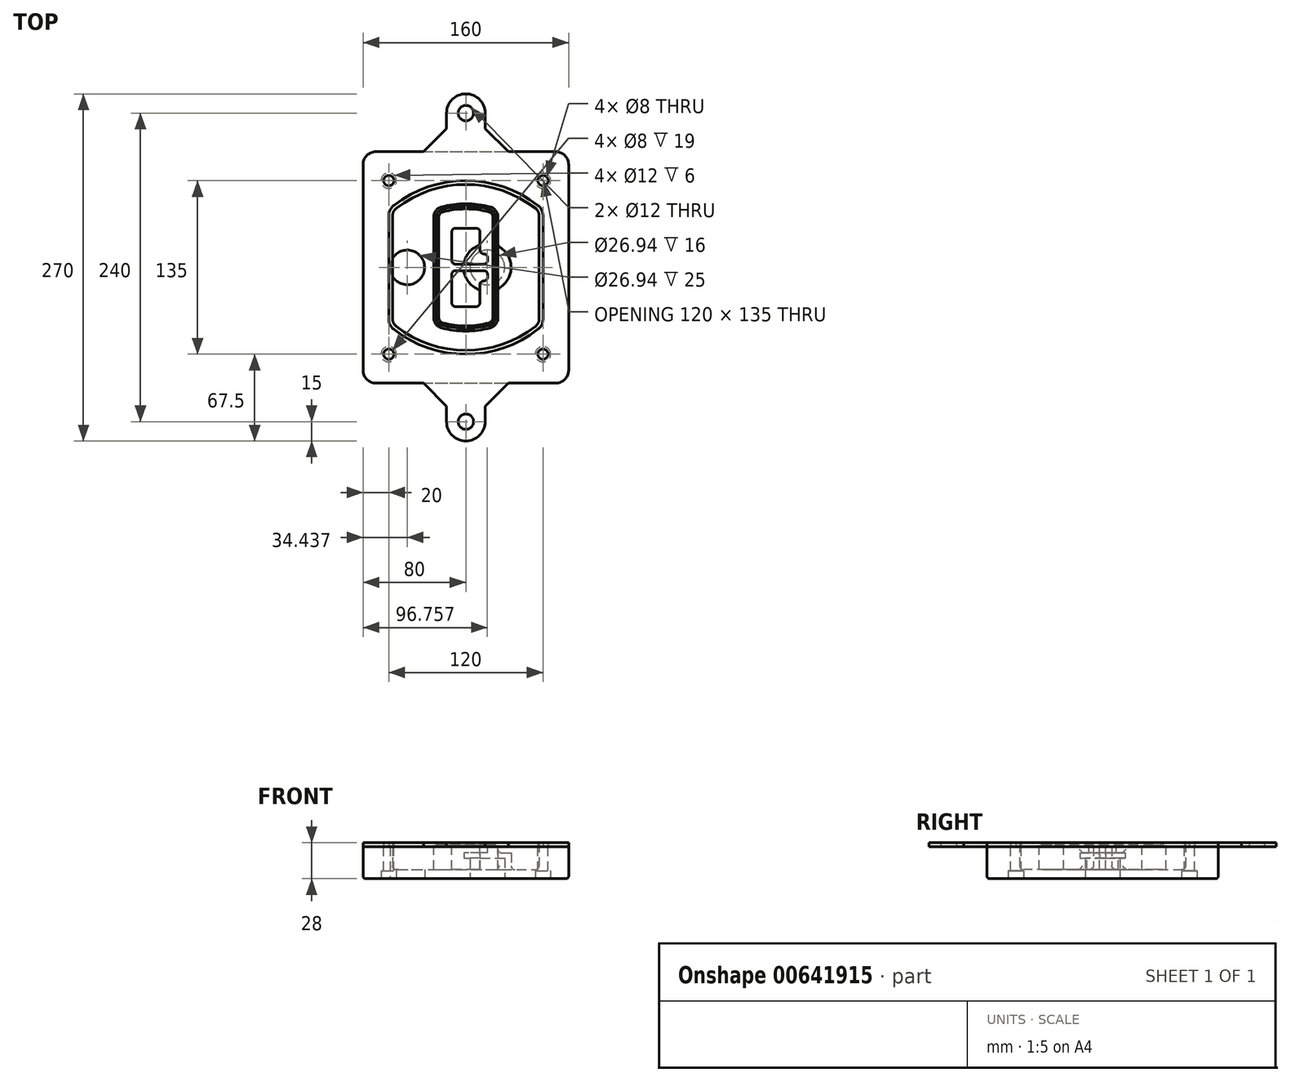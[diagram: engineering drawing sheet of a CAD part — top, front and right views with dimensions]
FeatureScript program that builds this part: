
annotation { "Feature Type Name" : "Feature", "Feature Type Description" : "" }
export const myFeature = defineFeature(function(context is Context, id is Id, definition is map)
    precondition{}
    {
        {
            var Q0;
            Q0=qCreatedBy(makeId("Top.planeOp"),FACE);
            var sketch = newSketch(context, id + "F0", { "sketchPlane" : qUnion([Q0])});
            skPoint(sketch, "E0.rect.middle", {"position": v(0, 0) * mm});
            skLineSegment(sketch, "E1.bottom", {"start": v(-70, -90) * mm, "end": v(70, -90) * mm});
            skLineSegment(sketch, "E1.top", {"start": v(-70, 90) * mm, "end": v(70, 90) * mm});
            skLineSegment(sketch, "E1.left", {"start": v(-80, -80) * mm, "end": v(-80, 80) * mm});
            skLineSegment(sketch, "E1.right", {"start": v(80, -80) * mm, "end": v(80, 80) * mm});
            skLineSegment(sketch, "E2", {"start": v(-80, 90) * mm, "end": v(80, -90) * mm, "construction": true});
            skLineSegment(sketch, "E3", {"start": v(80, 90) * mm, "end": v(-80, -90) * mm, "construction": true});
            skCircle(sketch, "E4", {"center": v(-60, 67.5) * mm, "radius": 4 * mm});
            skCircle(sketch, "E5", {"center": v(60, 67.5) * mm, "radius": 4 * mm});
            skCircle(sketch, "E6", {"center": v(60, -67.5) * mm, "radius": 4 * mm});
            skCircle(sketch, "E7", {"center": v(-60, -67.5) * mm, "radius": 4 * mm});
            skLineSegment(sketch, "E8", {"start": v(-60, 67.5) * mm, "end": v(60, 67.5) * mm, "construction": true});
            skLineSegment(sketch, "E9", {"start": v(60, 67.5) * mm, "end": v(60, -67.5) * mm, "construction": true});
            skLineSegment(sketch, "E10", {"start": v(60, -67.5) * mm, "end": v(-60, -67.5) * mm, "construction": true});
            skLineSegment(sketch, "E11", {"start": v(-60, -67.5) * mm, "end": v(-60, 67.5) * mm, "construction": true});
            skLineSegment(sketch, "E12", {"start": v(-60, 40.3) * mm, "end": v(-60, -40.3) * mm});
            skLineSegment(sketch, "E13", {"start": v(60, 40.3) * mm, "end": v(60, -40.3) * mm});
            skArc(sketch, "E14", {"start": v(56.15, 48.18) * mm, "mid": v(0, 67.5) * mm, "end": v(-56.15, 48.18) * mm});
            skArc(sketch, "E15", {"start": v(-56.15, -48.18) * mm, "mid": v(0, -67.5) * mm, "end": v(56.15, -48.18) * mm});
            skLineSegment(sketch, "E16", {"start": v(-60, 0) * mm, "end": v(60, 0) * mm, "construction": true});
            skPoint(sketch, "E17.visualSharp", {"position": v(-60, -45) * mm});
            skArc(sketch, "E17.filletArc", {"start": v(-60, -40.3) * mm, "mid": v(-58.99, -44.68) * mm, "end": v(-56.15, -48.18) * mm});
            skPoint(sketch, "E18.visualSharp", {"position": v(-60, 45) * mm});
            skArc(sketch, "E18.filletArc", {"start": v(-56.15, 48.18) * mm, "mid": v(-58.99, 44.68) * mm, "end": v(-60, 40.3) * mm});
            skPoint(sketch, "E19.visualSharp", {"position": v(60, 45) * mm});
            skArc(sketch, "E19.filletArc", {"start": v(60, 40.3) * mm, "mid": v(58.99, 44.68) * mm, "end": v(56.15, 48.18) * mm});
            skPoint(sketch, "E20.visualSharp", {"position": v(60, -45) * mm});
            skArc(sketch, "E20.filletArc", {"start": v(56.15, -48.18) * mm, "mid": v(58.99, -44.68) * mm, "end": v(60, -40.3) * mm});
            skPoint(sketch, "E21.visualSharp", {"position": v(-80, 90) * mm});
            skArc(sketch, "E21.filletArc", {"start": v(-70, 90) * mm, "mid": v(-77.07, 87.07) * mm, "end": v(-80, 80) * mm});
            skPoint(sketch, "E22.visualSharp", {"position": v(80, 90) * mm});
            skArc(sketch, "E22.filletArc", {"start": v(80, 80) * mm, "mid": v(77.07, 87.07) * mm, "end": v(70, 90) * mm});
            skPoint(sketch, "E23.visualSharp", {"position": v(80, -90) * mm});
            skArc(sketch, "E23.filletArc", {"start": v(70, -90) * mm, "mid": v(77.07, -87.07) * mm, "end": v(80, -80) * mm});
            skPoint(sketch, "E24.visualSharp", {"position": v(-80, -90) * mm});
            skArc(sketch, "E24.filletArc", {"start": v(-80, -80) * mm, "mid": v(-77.07, -87.07) * mm, "end": v(-70, -90) * mm});
            skArc(sketch, "E25.0", {"start": v(57, 40.3) * mm, "mid": v(56.3, 43.36) * mm, "end": v(54.3, 45.81) * mm});
            skLineSegment(sketch, "E25.1", {"start": v(57, 40.3) * mm, "end": v(57, -40.3) * mm});
            skArc(sketch, "E25.2", {"start": v(54.3, -45.81) * mm, "mid": v(56.3, -43.36) * mm, "end": v(57, -40.3) * mm});
            skArc(sketch, "E25.3", {"start": v(-54.3, -45.81) * mm, "mid": v(0, -64.5) * mm, "end": v(54.3, -45.81) * mm});
            skArc(sketch, "E25.4", {"start": v(-57, -40.3) * mm, "mid": v(-56.3, -43.36) * mm, "end": v(-54.3, -45.81) * mm});
            skArc(sketch, "E25.5", {"start": v(54.3, 45.81) * mm, "mid": v(0, 64.5) * mm, "end": v(-54.3, 45.81) * mm});
            skLineSegment(sketch, "E25.6", {"start": v(-57, 40.3) * mm, "end": v(-57, -40.3) * mm});
            skArc(sketch, "E25.7", {"start": v(-54.3, 45.81) * mm, "mid": v(-56.3, 43.36) * mm, "end": v(-57, 40.3) * mm});
            skArc(sketch, "E26.0", {"start": v(-58.62, 51.33) * mm, "mid": v(-62.58, 46.43) * mm, "end": v(-64, 40.3) * mm});
            skArc(sketch, "E26.1", {"start": v(58.62, 51.33) * mm, "mid": v(0, 71.5) * mm, "end": v(-58.62, 51.33) * mm});
            skArc(sketch, "E26.2", {"start": v(64, 40.3) * mm, "mid": v(62.58, 46.43) * mm, "end": v(58.62, 51.33) * mm});
            skLineSegment(sketch, "E26.3", {"start": v(64, 40.3) * mm, "end": v(64, -40.3) * mm});
            skArc(sketch, "E26.4", {"start": v(58.62, -51.33) * mm, "mid": v(62.58, -46.43) * mm, "end": v(64, -40.3) * mm});
            skLineSegment(sketch, "E26.5", {"start": v(-64, 40.3) * mm, "end": v(-64, -40.3) * mm});
            skArc(sketch, "E26.6", {"start": v(-58.62, -51.33) * mm, "mid": v(0, -71.5) * mm, "end": v(58.62, -51.33) * mm});
            skArc(sketch, "E26.7", {"start": v(-64, -40.3) * mm, "mid": v(-62.58, -46.43) * mm, "end": v(-58.62, -51.33) * mm});
            skSolve(sketch);
        }
        {
            var Q0;
            Q0=makeQuery(id+"F0.imprint","IMPRINT",FACE,{"disambiguationData":[TD([[makeQuery(id+"F0.imprint","IMPRINT",EDGE,{"derivedFrom":sQuery(id+"F0.wireOp",EDGE,"E1.bottom")}),1.0]])]});
            var Q1;
            Q1=makeQuery(id+"F0.imprint","IMPRINT",FACE,{"disambiguationData":[TD([[makeQuery(id+"F0.imprint","IMPRINT",EDGE,{"derivedFrom":sQuery(id+"F0.wireOp",EDGE,"E12")}),1.0]])]});
            var Q2;
            Q2=makeQuery(id+"F0.imprint","IMPRINT",FACE,{"disambiguationData":[TD([[makeQuery(id+"F0.imprint","IMPRINT",EDGE,{"derivedFrom":sQuery(id+"F0.wireOp",EDGE,"E25.0")}),1.0]])]});
            var Q3;
            Q3=makeQuery(id+"F0.imprint","IMPRINT",FACE,{"disambiguationData":[TD([[makeQuery(id+"F0.imprint","IMPRINT",EDGE,{"derivedFrom":sQuery(id+"F0.wireOp",EDGE,"E12")}),-1.0]])]});
            extrude(context, id + "F1", {"entities" : qUnion([Q0, Q1, Q2, Q3]), "oppositeDirection" : true, "depth" : 25 * mm});
        }
        {
            var Q0;
            Q0=makeQuery(id+"F0.imprint","IMPRINT",FACE,{"disambiguationData":[TD([[makeQuery(id+"F0.imprint","IMPRINT",EDGE,{"derivedFrom":sQuery(id+"F0.wireOp",EDGE,"E12")}),1.0]])]});
            extrude(context, id + "F2", {"entities" : qUnion([Q0]), "operationType" : NewBodyOperationType.ADD, "depth" : 3 * mm});
        }
        {
            var Q0;
            Q0=makeQuery(id+"F0.imprint","IMPRINT",FACE,{"disambiguationData":[TD([[makeQuery(id+"F0.imprint","IMPRINT",EDGE,{"derivedFrom":sQuery(id+"F0.wireOp",EDGE,"E25.0")}),1.0]])]});
            extrude(context, id + "F3", {"entities" : qUnion([Q0]), "operationType" : NewBodyOperationType.REMOVE, "oppositeDirection" : true, "depth" : 18 * mm});
        }
        {
            var Q0;
            Q0=makeQuery(id+"F2.opExtrude","CAP_FACE",FACE,{"disambiguationData":[OSD([sQuery(id+"F0.wireOp",EDGE,"E12"),sQuery(id+"F0.wireOp",EDGE,"E13"),sQuery(id+"F0.wireOp",EDGE,"E14"),sQuery(id+"F0.wireOp",EDGE,"E15"),sQuery(id+"F0.wireOp",EDGE,"E17.filletArc"),sQuery(id+"F0.wireOp",EDGE,"E18.filletArc"),sQuery(id+"F0.wireOp",EDGE,"E19.filletArc"),sQuery(id+"F0.wireOp",EDGE,"E20.filletArc"),sQuery(id+"F0.wireOp",EDGE,"E25.0"),sQuery(id+"F0.wireOp",EDGE,"E25.1"),sQuery(id+"F0.wireOp",EDGE,"E25.2"),sQuery(id+"F0.wireOp",EDGE,"E25.3"),sQuery(id+"F0.wireOp",EDGE,"E25.4"),sQuery(id+"F0.wireOp",EDGE,"E25.5"),sQuery(id+"F0.wireOp",EDGE,"E25.6"),sQuery(id+"F0.wireOp",EDGE,"E25.7")])],"isStart":false});
            var sketch = newSketch(context, id + "F4", { "sketchPlane" : qUnion([Q0])});
            skArc(sketch, "E27.0", {"start": v(-19.08, -46.97) * mm, "mid": v(0, -49.5) * mm, "end": v(19.08, -46.97) * mm});
            skArc(sketch, "E28.0", {"start": v(19.08, 46.97) * mm, "mid": v(0, 49.5) * mm, "end": v(-19.08, 46.97) * mm});
            skLineSegment(sketch, "E29", {"start": v(-25, 39.25) * mm, "end": v(-25, -39.25) * mm});
            skLineSegment(sketch, "E30", {"start": v(25, 39.25) * mm, "end": v(25, -39.25) * mm});
            skLineSegment(sketch, "E31", {"start": v(-25, 45.1) * mm, "end": v(25, 45.1) * mm, "construction": true});
            skLineSegment(sketch, "E32", {"start": v(-25, -45.1) * mm, "end": v(25, -45.1) * mm, "construction": true});
            skPoint(sketch, "E33.visualSharp", {"position": v(-25, 45.1) * mm});
            skArc(sketch, "E33.filletArc", {"start": v(-19.08, 46.97) * mm, "mid": v(-23.35, 44.11) * mm, "end": v(-25, 39.25) * mm});
            skPoint(sketch, "E34.visualSharp", {"position": v(25, 45.1) * mm});
            skArc(sketch, "E34.filletArc", {"start": v(25, 39.25) * mm, "mid": v(23.35, 44.11) * mm, "end": v(19.08, 46.97) * mm});
            skPoint(sketch, "E35.visualSharp", {"position": v(25, -45.1) * mm});
            skArc(sketch, "E35.filletArc", {"start": v(19.08, -46.97) * mm, "mid": v(23.35, -44.11) * mm, "end": v(25, -39.25) * mm});
            skPoint(sketch, "E36.visualSharp", {"position": v(-25, -45.1) * mm});
            skArc(sketch, "E36.filletArc", {"start": v(-25, -39.25) * mm, "mid": v(-23.35, -44.11) * mm, "end": v(-19.08, -46.97) * mm});
            skArc(sketch, "E37.0", {"start": v(54.3, 45.81) * mm, "mid": v(0, 64.5) * mm, "end": v(-54.3, 45.81) * mm});
            skArc(sketch, "E37.1", {"start": v(-54.3, 45.81) * mm, "mid": v(-56.3, 43.36) * mm, "end": v(-57, 40.3) * mm});
            skLineSegment(sketch, "E37.2", {"start": v(-57, 40.3) * mm, "end": v(-57, -40.3) * mm});
            skArc(sketch, "E37.3", {"start": v(-57, -40.3) * mm, "mid": v(-56.3, -43.36) * mm, "end": v(-54.3, -45.81) * mm});
            skArc(sketch, "E37.4", {"start": v(-54.3, -45.81) * mm, "mid": v(0, -64.5) * mm, "end": v(54.3, -45.81) * mm});
            skArc(sketch, "E37.5", {"start": v(54.3, -45.81) * mm, "mid": v(56.3, -43.36) * mm, "end": v(57, -40.3) * mm});
            skLineSegment(sketch, "E37.6", {"start": v(57, 40.3) * mm, "end": v(57, -40.3) * mm});
            skArc(sketch, "E37.7", {"start": v(57, 40.3) * mm, "mid": v(56.3, 43.36) * mm, "end": v(54.3, 45.81) * mm});
            skLineSegment(sketch, "E38.0", {"start": v(23, 39.25) * mm, "end": v(23, -39.25) * mm});
            skArc(sketch, "E38.1", {"start": v(18.56, -45.04) * mm, "mid": v(21.76, -42.9) * mm, "end": v(23, -39.25) * mm});
            skArc(sketch, "E38.2", {"start": v(-18.56, -45.04) * mm, "mid": v(0, -47.5) * mm, "end": v(18.56, -45.04) * mm});
            skArc(sketch, "E38.3", {"start": v(-23, -39.25) * mm, "mid": v(-21.76, -42.9) * mm, "end": v(-18.56, -45.04) * mm});
            skLineSegment(sketch, "E38.4", {"start": v(-23, 39.25) * mm, "end": v(-23, -39.25) * mm});
            skArc(sketch, "E38.5", {"start": v(23, 39.25) * mm, "mid": v(21.76, 42.9) * mm, "end": v(18.56, 45.04) * mm});
            skArc(sketch, "E38.6", {"start": v(-18.56, 45.04) * mm, "mid": v(-21.76, 42.9) * mm, "end": v(-23, 39.25) * mm});
            skArc(sketch, "E38.7", {"start": v(18.56, 45.04) * mm, "mid": v(0, 47.5) * mm, "end": v(-18.56, 45.04) * mm});
            skArc(sketch, "E39.0", {"start": v(21, 39.25) * mm, "mid": v(20.18, 41.68) * mm, "end": v(18.04, 43.1) * mm});
            skLineSegment(sketch, "E39.1", {"start": v(21, 39.25) * mm, "end": v(21, -39.25) * mm});
            skArc(sketch, "E39.2", {"start": v(18.04, -43.1) * mm, "mid": v(20.18, -41.68) * mm, "end": v(21, -39.25) * mm});
            skArc(sketch, "E39.3", {"start": v(-18.04, -43.1) * mm, "mid": v(0, -45.5) * mm, "end": v(18.04, -43.1) * mm});
            skArc(sketch, "E39.4", {"start": v(-21, -39.25) * mm, "mid": v(-20.18, -41.68) * mm, "end": v(-18.04, -43.1) * mm});
            skArc(sketch, "E39.5", {"start": v(18.04, 43.1) * mm, "mid": v(0, 45.5) * mm, "end": v(-18.04, 43.1) * mm});
            skLineSegment(sketch, "E39.6", {"start": v(-21, 39.25) * mm, "end": v(-21, -39.25) * mm});
            skArc(sketch, "E39.7", {"start": v(-18.04, 43.1) * mm, "mid": v(-20.18, 41.68) * mm, "end": v(-21, 39.25) * mm});
            skLineSegment(sketch, "E40", {"start": v(-25, 0) * mm, "end": v(25, 0) * mm, "construction": true});
            skLineSegment(sketch, "E41", {"start": v(-11, 5.5) * mm, "end": v(-11, 27.5) * mm});
            skLineSegment(sketch, "E42", {"start": v(-8, 30.5) * mm, "end": v(8, 30.5) * mm});
            skLineSegment(sketch, "E43", {"start": v(11, 27.5) * mm, "end": v(11, 13.5) * mm});
            skLineSegment(sketch, "E44", {"start": v(14, 10.5) * mm, "end": v(14, 10.5) * mm});
            skLineSegment(sketch, "E45", {"start": v(17, 7.5) * mm, "end": v(17, 5.5) * mm});
            skLineSegment(sketch, "E46", {"start": v(14, 2.5) * mm, "end": v(-8, 2.5) * mm});
            skPoint(sketch, "E47.visualSharp", {"position": v(-11, 30.5) * mm});
            skArc(sketch, "E47.filletArc", {"start": v(-8, 30.5) * mm, "mid": v(-10.12, 29.62) * mm, "end": v(-11, 27.5) * mm});
            skPoint(sketch, "E48.visualSharp", {"position": v(11, 30.5) * mm});
            skArc(sketch, "E48.filletArc", {"start": v(11, 27.5) * mm, "mid": v(10.12, 29.62) * mm, "end": v(8, 30.5) * mm});
            skPoint(sketch, "E49.visualSharp", {"position": v(11, 10.5) * mm});
            skArc(sketch, "E49.filletArc", {"start": v(11, 13.5) * mm, "mid": v(11.88, 11.38) * mm, "end": v(14, 10.5) * mm});
            skPoint(sketch, "E50.visualSharp", {"position": v(17, 10.5) * mm});
            skArc(sketch, "E50.filletArc", {"start": v(17, 7.5) * mm, "mid": v(16.12, 9.62) * mm, "end": v(14, 10.5) * mm});
            skPoint(sketch, "E51.visualSharp", {"position": v(17, 2.5) * mm});
            skArc(sketch, "E51.filletArc", {"start": v(14, 2.5) * mm, "mid": v(16.12, 3.38) * mm, "end": v(17, 5.5) * mm});
            skPoint(sketch, "E52.visualSharp", {"position": v(-11, 2.5) * mm});
            skArc(sketch, "E52.filletArc", {"start": v(-11, 5.5) * mm, "mid": v(-10.12, 3.38) * mm, "end": v(-8, 2.5) * mm});
            skLineSegment(sketch, "E53.0.MirrorCS", {"start": v(14, -2.5) * mm, "end": v(-8, -2.5) * mm});
            skArc(sketch, "E54.0.MirrorCS", {"start": v(-11, -5.5) * mm, "mid": v(-10.12, -3.38) * mm, "end": v(-8, -2.5) * mm});
            skLineSegment(sketch, "E55.0.MirrorCS", {"start": v(-11, -5.5) * mm, "end": v(-11, -27.5) * mm});
            skArc(sketch, "E56.0.MirrorCS", {"start": v(-8, -30.5) * mm, "mid": v(-10.12, -29.62) * mm, "end": v(-11, -27.5) * mm});
            skLineSegment(sketch, "E57.0.MirrorCS", {"start": v(-8, -30.5) * mm, "end": v(8, -30.5) * mm});
            skArc(sketch, "E58.0.MirrorCS", {"start": v(11, -27.5) * mm, "mid": v(10.12, -29.62) * mm, "end": v(8, -30.5) * mm});
            skLineSegment(sketch, "E59.0.MirrorCS", {"start": v(11, -27.5) * mm, "end": v(11, -13.5) * mm});
            skArc(sketch, "E60.0.MirrorCS", {"start": v(11, -13.5) * mm, "mid": v(11.88, -11.38) * mm, "end": v(14, -10.5) * mm});
            skArc(sketch, "E61.0.MirrorCS", {"start": v(17, -7.5) * mm, "mid": v(16.12, -9.62) * mm, "end": v(14, -10.5) * mm});
            skLineSegment(sketch, "E62.0.MirrorCS", {"start": v(17, -7.5) * mm, "end": v(17, -5.5) * mm});
            skArc(sketch, "E63.0.MirrorCS", {"start": v(14, -2.5) * mm, "mid": v(16.12, -3.38) * mm, "end": v(17, -5.5) * mm});
            skSolve(sketch);
        }
        {
            var Q0;
            Q0=makeQuery(id+"F4.imprint","IMPRINT",FACE,{"disambiguationData":[TD([[makeQuery(id+"F4.imprint","IMPRINT",EDGE,{"derivedFrom":sQuery(id+"F4.wireOp",EDGE,"E27.0")}),1.0]])]});
            var Q1;
            Q1=makeQuery(id+"F4.imprint","IMPRINT",FACE,{"disambiguationData":[TD([[makeQuery(id+"F4.imprint","IMPRINT",EDGE,{"derivedFrom":sQuery(id+"F4.wireOp",EDGE,"E38.0")}),-1.0]])]});
            var Q2;
            Q2=makeQuery(id+"F4.imprint","IMPRINT",FACE,{"disambiguationData":[TD([[makeQuery(id+"F4.imprint","IMPRINT",EDGE,{"derivedFrom":sQuery(id+"F4.wireOp",EDGE,"E39.0")}),1.0]])]});
            extrude(context, id + "F5", {"entities" : qUnion([Q0, Q1, Q2]), "operationType" : NewBodyOperationType.ADD, "endBound" : BoundingType.UP_TO_NEXT, "oppositeDirection" : true, "depth" : 25 * mm});
        }
        {
            var Q0;
            Q0=makeQuery(id+"F4.imprint","IMPRINT",FACE,{"disambiguationData":[TD([[makeQuery(id+"F4.imprint","IMPRINT",EDGE,{"derivedFrom":sQuery(id+"F4.wireOp",EDGE,"E38.0")}),-1.0]])]});
            extrude(context, id + "F6", {"entities" : qUnion([Q0]), "operationType" : NewBodyOperationType.REMOVE, "oppositeDirection" : true, "depth" : 2 * mm});
        }
        {
            var Q0;
            Q0=makeQuery(id+"F1.opExtrude","CAP_FACE",FACE,{"disambiguationData":[OSD([sQuery(id+"F0.wireOp",EDGE,"E1.bottom"),sQuery(id+"F0.wireOp",EDGE,"E1.top"),sQuery(id+"F0.wireOp",EDGE,"E1.left"),sQuery(id+"F0.wireOp",EDGE,"E1.right"),sQuery(id+"F0.wireOp",EDGE,"E4"),sQuery(id+"F0.wireOp",EDGE,"E5"),sQuery(id+"F0.wireOp",EDGE,"E6"),sQuery(id+"F0.wireOp",EDGE,"E7"),sQuery(id+"F0.wireOp",EDGE,"E21.filletArc"),sQuery(id+"F0.wireOp",EDGE,"E22.filletArc"),sQuery(id+"F0.wireOp",EDGE,"E23.filletArc"),sQuery(id+"F0.wireOp",EDGE,"E24.filletArc")])],"isStart":false});
            var sketch = newSketch(context, id + "F7", { "sketchPlane" : qUnion([Q0])});
            skCircle(sketch, "E64", {"center": v(16.76, 0) * mm, "radius": 13.47 * mm});
            skCircle(sketch, "E65", {"center": v(-45.56, 0) * mm, "radius": 13.47 * mm});
            skLineSegment(sketch, "E66", {"start": v(80, 0) * mm, "end": v(-80, 0) * mm});
            skCircle(sketch, "E67", {"center": v(16.76, 0) * mm, "radius": 18.47 * mm});
            skCircle(sketch, "E68", {"center": v(60, -67.5) * mm, "radius": 6 * mm});
            skCircle(sketch, "E69", {"center": v(-60, -67.5) * mm, "radius": 6 * mm});
            skCircle(sketch, "E70", {"center": v(-60, 67.5) * mm, "radius": 6 * mm});
            skCircle(sketch, "E71", {"center": v(60, 67.5) * mm, "radius": 6 * mm});
            skSolve(sketch);
        }
        {
            var Q0;
            {var subQ1=sQuery(id+"F7.wireOp",EDGE,"E66");var subQ4=sQuery(id+"F7.wireOp",EDGE,"E64");var subQ6=makeQuery(id+"F7.imprint","INTERSECT",VERTEX,{"disambiguationData":[OD(0.0)],"derivedFrom":[subQ4,subQ1]});Q0=makeQuery(id+"F7.imprint","IMPRINT",FACE,{"disambiguationData":[TD([[makeQuery(id+"F7.imprint","IMPRINT",EDGE,{"disambiguationData":[TD([[subQ6,-1.0]])],"derivedFrom":subQ4}),-1.0]])]});}
            var Q1;
            {var subQ0=sQuery(id+"F7.wireOp",EDGE,"E66");var subQ1=sQuery(id+"F7.wireOp",EDGE,"E64");var subQ3=makeQuery(id+"F7.imprint","INTERSECT",VERTEX,{"disambiguationData":[OD(0.0)],"derivedFrom":[subQ1,subQ0]});Q1=makeQuery(id+"F7.imprint","IMPRINT",FACE,{"disambiguationData":[TD([[makeQuery(id+"F7.imprint","IMPRINT",EDGE,{"disambiguationData":[TD([[subQ3,-1.0]])],"derivedFrom":subQ1}),1.0]])]});}
            var Q2;
            {var subQ0=sQuery(id+"F7.wireOp",EDGE,"E66");var subQ1=sQuery(id+"F7.wireOp",EDGE,"E64");var subQ3=makeQuery(id+"F7.imprint","INTERSECT",VERTEX,{"disambiguationData":[OD(0.0)],"derivedFrom":[subQ1,subQ0]});Q2=makeQuery(id+"F7.imprint","IMPRINT",FACE,{"disambiguationData":[TD([[makeQuery(id+"F7.imprint","IMPRINT",EDGE,{"disambiguationData":[TD([[subQ3,1.0]])],"derivedFrom":subQ1}),1.0]])]});}
            var Q3;
            {var subQ1=sQuery(id+"F7.wireOp",EDGE,"E66");var subQ4=sQuery(id+"F7.wireOp",EDGE,"E64");var subQ6=makeQuery(id+"F7.imprint","INTERSECT",VERTEX,{"disambiguationData":[OD(0.0)],"derivedFrom":[subQ4,subQ1]});Q3=makeQuery(id+"F7.imprint","IMPRINT",FACE,{"disambiguationData":[TD([[makeQuery(id+"F7.imprint","IMPRINT",EDGE,{"disambiguationData":[TD([[subQ6,1.0]])],"derivedFrom":subQ4}),-1.0]])]});}
            extrude(context, id + "F8", {"entities" : qUnion([Q0, Q1, Q2, Q3]), "operationType" : NewBodyOperationType.ADD, "oppositeDirection" : true, "depth" : 20 * mm});
        }
        {
            var Q0;
            {var subQ0=sQuery(id+"F7.wireOp",EDGE,"E66");var subQ1=sQuery(id+"F7.wireOp",EDGE,"E64");var subQ3=makeQuery(id+"F7.imprint","INTERSECT",VERTEX,{"disambiguationData":[OD(0.0)],"derivedFrom":[subQ1,subQ0]});Q0=makeQuery(id+"F7.imprint","IMPRINT",FACE,{"disambiguationData":[TD([[makeQuery(id+"F7.imprint","IMPRINT",EDGE,{"disambiguationData":[TD([[subQ3,-1.0]])],"derivedFrom":subQ1}),1.0]])]});}
            var Q1;
            {var subQ0=sQuery(id+"F7.wireOp",EDGE,"E66");var subQ1=sQuery(id+"F7.wireOp",EDGE,"E64");var subQ3=makeQuery(id+"F7.imprint","INTERSECT",VERTEX,{"disambiguationData":[OD(0.0)],"derivedFrom":[subQ1,subQ0]});Q1=makeQuery(id+"F7.imprint","IMPRINT",FACE,{"disambiguationData":[TD([[makeQuery(id+"F7.imprint","IMPRINT",EDGE,{"disambiguationData":[TD([[subQ3,1.0]])],"derivedFrom":subQ1}),1.0]])]});}
            extrude(context, id + "F9", {"entities" : qUnion([Q0, Q1]), "operationType" : NewBodyOperationType.REMOVE, "oppositeDirection" : true, "depth" : 16 * mm});
        }
        {
            var Q0;
            {var subQ0=sQuery(id+"F7.wireOp",EDGE,"E66");var subQ1=sQuery(id+"F7.wireOp",EDGE,"E65");var subQ3=makeQuery(id+"F7.imprint","INTERSECT",VERTEX,{"disambiguationData":[OD(0.0)],"derivedFrom":[subQ1,subQ0]});Q0=makeQuery(id+"F7.imprint","IMPRINT",FACE,{"disambiguationData":[TD([[makeQuery(id+"F7.imprint","IMPRINT",EDGE,{"disambiguationData":[TD([[subQ3,-1.0]])],"derivedFrom":subQ1}),1.0]])]});}
            var Q1;
            {var subQ0=sQuery(id+"F7.wireOp",EDGE,"E66");var subQ1=sQuery(id+"F7.wireOp",EDGE,"E65");var subQ3=makeQuery(id+"F7.imprint","INTERSECT",VERTEX,{"disambiguationData":[OD(0.0)],"derivedFrom":[subQ1,subQ0]});Q1=makeQuery(id+"F7.imprint","IMPRINT",FACE,{"disambiguationData":[TD([[makeQuery(id+"F7.imprint","IMPRINT",EDGE,{"disambiguationData":[TD([[subQ3,1.0]])],"derivedFrom":subQ1}),1.0]])]});}
            extrude(context, id + "F10", {"entities" : qUnion([Q0, Q1]), "operationType" : NewBodyOperationType.REMOVE, "oppositeDirection" : true, "depth" : 25 * mm});
        }
        {
            var Q0;
            Q0=makeQuery(id+"F7.imprint","IMPRINT",FACE,{"disambiguationData":[TD([[makeQuery(id+"F7.imprint","IMPRINT",EDGE,{"derivedFrom":sQuery(id+"F7.wireOp",EDGE,"E68")}),1.0]])]});
            var Q1;
            Q1=makeQuery(id+"F7.imprint","IMPRINT",FACE,{"disambiguationData":[TD([[makeQuery(id+"F7.imprint","IMPRINT",EDGE,{"derivedFrom":makeQuery(id+"F1.opExtrude","CAP_EDGE",EDGE,{"disambiguationData":[OSD([sQuery(id+"F0.wireOp",EDGE,"E5")])],"isStart":false})}),-1.0]])]});
            var Q2;
            Q2=makeQuery(id+"F7.imprint","IMPRINT",FACE,{"disambiguationData":[TD([[makeQuery(id+"F7.imprint","IMPRINT",EDGE,{"derivedFrom":sQuery(id+"F7.wireOp",EDGE,"E69")}),1.0]])]});
            var Q3;
            Q3=makeQuery(id+"F7.imprint","IMPRINT",FACE,{"disambiguationData":[TD([[makeQuery(id+"F7.imprint","IMPRINT",EDGE,{"derivedFrom":makeQuery(id+"F1.opExtrude","CAP_EDGE",EDGE,{"disambiguationData":[OSD([sQuery(id+"F0.wireOp",EDGE,"E4")])],"isStart":false})}),-1.0]])]});
            var Q4;
            Q4=makeQuery(id+"F7.imprint","IMPRINT",FACE,{"disambiguationData":[TD([[makeQuery(id+"F7.imprint","IMPRINT",EDGE,{"derivedFrom":sQuery(id+"F7.wireOp",EDGE,"E70")}),1.0]])]});
            var Q5;
            Q5=makeQuery(id+"F7.imprint","IMPRINT",FACE,{"disambiguationData":[TD([[makeQuery(id+"F7.imprint","IMPRINT",EDGE,{"derivedFrom":makeQuery(id+"F1.opExtrude","CAP_EDGE",EDGE,{"disambiguationData":[OSD([sQuery(id+"F0.wireOp",EDGE,"E7")])],"isStart":false})}),-1.0]])]});
            var Q6;
            Q6=makeQuery(id+"F7.imprint","IMPRINT",FACE,{"disambiguationData":[TD([[makeQuery(id+"F7.imprint","IMPRINT",EDGE,{"derivedFrom":sQuery(id+"F7.wireOp",EDGE,"E71")}),1.0]])]});
            var Q7;
            Q7=makeQuery(id+"F7.imprint","IMPRINT",FACE,{"disambiguationData":[TD([[makeQuery(id+"F7.imprint","IMPRINT",EDGE,{"derivedFrom":makeQuery(id+"F1.opExtrude","CAP_EDGE",EDGE,{"disambiguationData":[OSD([sQuery(id+"F0.wireOp",EDGE,"E6")])],"isStart":false})}),-1.0]])]});
            extrude(context, id + "F11", {"entities" : qUnion([Q0, Q1, Q2, Q3, Q4, Q5, Q6, Q7]), "operationType" : NewBodyOperationType.REMOVE, "oppositeDirection" : true, "depth" : 6 * mm});
        }
        {
            var Q0;
            Q0=makeQuery(id+"F9.boolean.opBoolean","COPY",FACE,{"derivedFrom":makeQuery(id+"F9.opExtrude","CAP_FACE",FACE,{"disambiguationData":[OSD([sQuery(id+"F7.wireOp",EDGE,"E64")])],"isStart":false})});
            var sketch = newSketch(context, id + "F12", { "sketchPlane" : qUnion([Q0])});
            skArc(sketch, "E72.0", {"start": v(11, 17.55) * mm, "mid": v(2.57, 11.82) * mm, "end": v(-1.54, 2.5) * mm});
            skArc(sketch, "E72.1", {"start": v(-1.54, -2.5) * mm, "mid": v(2.57, -11.82) * mm, "end": v(11, -17.55) * mm});
            skLineSegment(sketch, "E73", {"start": v(-1.54, -2.5) * mm, "end": v(14, -2.5) * mm});
            skLineSegment(sketch, "E74.0", {"start": v(14, 2.5) * mm, "end": v(-1.54, 2.5) * mm});
            skArc(sketch, "E74.1", {"start": v(14, 2.5) * mm, "mid": v(16.12, 3.38) * mm, "end": v(17, 5.5) * mm});
            skLineSegment(sketch, "E74.2", {"start": v(17, 7.5) * mm, "end": v(17, 5.5) * mm});
            skArc(sketch, "E74.3", {"start": v(17, 7.5) * mm, "mid": v(16.12, 9.62) * mm, "end": v(14, 10.5) * mm});
            skArc(sketch, "E74.4", {"start": v(11, 13.5) * mm, "mid": v(11.88, 11.38) * mm, "end": v(14, 10.5) * mm});
            skLineSegment(sketch, "E74.5", {"start": v(11, 17.55) * mm, "end": v(11, 13.5) * mm});
            skLineSegment(sketch, "E74.7", {"start": v(14, -2.5) * mm, "end": v(-1.54, -2.5) * mm});
            skArc(sketch, "E74.8", {"start": v(14, -2.5) * mm, "mid": v(16.12, -3.38) * mm, "end": v(17, -5.5) * mm});
            skLineSegment(sketch, "E74.9", {"start": v(17, -7.5) * mm, "end": v(17, -5.5) * mm});
            skArc(sketch, "E74.10", {"start": v(17, -7.5) * mm, "mid": v(16.12, -9.62) * mm, "end": v(14, -10.5) * mm});
            skArc(sketch, "E74.11", {"start": v(11, -13.5) * mm, "mid": v(11.88, -11.38) * mm, "end": v(14, -10.5) * mm});
            skLineSegment(sketch, "E74.12", {"start": v(11, -17.55) * mm, "end": v(11, -13.5) * mm});
            skPoint(sketch, "E75.orphan", {"position": v(11, -27.5) * mm});
            skPoint(sketch, "E76.orphan", {"position": v(-8, -2.5) * mm});
            skPoint(sketch, "E77.orphan", {"position": v(-8, 2.5) * mm});
            skPoint(sketch, "E78.orphan", {"position": v(11, 27.5) * mm});
            skSolve(sketch);
        }
        {
            var Q0;
            {var subQ7=sQuery(id+"F12.wireOp",EDGE,"E72.0");var subQ14=sQuery(id+"F12.wireOp",EDGE,"E72.1");var subQ16=sQuery(id+"F12.wireOp",EDGE,"E74.1");var subQ18=sQuery(id+"F12.wireOp",EDGE,"E74.8");Q0=qUnion([makeQuery(id+"F12.imprint","IMPRINT",FACE,{"disambiguationData":[TD([[makeQuery(id+"F12.imprint","IMPRINT",EDGE,{"derivedFrom":subQ7}),1.0]])]}),makeQuery(id+"F12.imprint","IMPRINT",FACE,{"disambiguationData":[TD([[makeQuery(id+"F12.imprint","IMPRINT",EDGE,{"derivedFrom":subQ14}),1.0]])]}),makeQuery(id+"F12.imprint","IMPRINT",FACE,{"disambiguationData":[TD([[makeQuery(id+"F12.imprint","IMPRINT",EDGE,{"derivedFrom":subQ16}),1.0]])]}),makeQuery(id+"F12.imprint","IMPRINT",FACE,{"disambiguationData":[TD([[makeQuery(id+"F12.imprint","IMPRINT",EDGE,{"derivedFrom":subQ18}),-1.0]])]})]);}
            var Q1;
            Q1=makeQuery(id+"F5.boolean.opBoolean","SPLIT",FACE,{"disambiguationData":[TD([makeQuery(id+"F5.opExtrude","SWEPT_FACE",FACE,{"disambiguationData":[OSD([sQuery(id+"F4.wireOp",EDGE,"E41")])]})])],"derivedFrom":makeQuery(id+"F3.boolean.opBoolean","COPY",FACE,{"derivedFrom":makeQuery(id+"F3.opExtrude","CAP_FACE",FACE,{"disambiguationData":[OSD([sQuery(id+"F0.wireOp",EDGE,"E25.0"),sQuery(id+"F0.wireOp",EDGE,"E25.1"),sQuery(id+"F0.wireOp",EDGE,"E25.2"),sQuery(id+"F0.wireOp",EDGE,"E25.3"),sQuery(id+"F0.wireOp",EDGE,"E25.4"),sQuery(id+"F0.wireOp",EDGE,"E25.5"),sQuery(id+"F0.wireOp",EDGE,"E25.6"),sQuery(id+"F0.wireOp",EDGE,"E25.7")])],"isStart":false})})});
            extrude(context, id + "F13", {"entities" : qUnion([Q0]), "operationType" : NewBodyOperationType.REMOVE, "endBound" : BoundingType.UP_TO_SURFACE, "endBoundEntityFace" : qUnion([Q1]), "depth" : 25 * mm});
        }
        {
            var Q0;
            Q0=makeQuery(id+"F3.boolean.opBoolean","COPY",EDGE,{"derivedFrom":makeQuery(id+"F3.opExtrude","CAP_EDGE",EDGE,{"disambiguationData":[OSD([sQuery(id+"F0.wireOp",EDGE,"E25.6")])],"isStart":false})});
            var Q1;
            Q1=makeQuery(id+"F8.boolean.opBoolean","INTERSECT",EDGE,{"derivedFrom":[makeQuery(id+"F5.opExtrude","SWEPT_FACE",FACE,{"disambiguationData":[OSD([sQuery(id+"F4.wireOp",EDGE,"E30")])]}),makeQuery(id+"F8.opExtrude","CAP_FACE",FACE,{"disambiguationData":[OSD([sQuery(id+"F7.wireOp",EDGE,"E67")])],"isStart":false})]});
            var Q2;
            Q2=makeQuery(id+"F8.boolean.opBoolean","INTERSECT",EDGE,{"disambiguationData":[OD(1.0)],"derivedFrom":[makeQuery(id+"F5.opExtrude","SWEPT_FACE",FACE,{"disambiguationData":[OSD([sQuery(id+"F4.wireOp",EDGE,"E30")])]}),makeQuery(id+"F8.opExtrude","SWEPT_FACE",FACE,{"disambiguationData":[OSD([sQuery(id+"F7.wireOp",EDGE,"E67")])]})]});
            var Q3;
            {var subQ0=sQuery(id+"F4.wireOp",EDGE,"E30");Q3=makeQuery(id+"F8.boolean.opBoolean","SPLIT",EDGE,{"disambiguationData":[TD([makeQuery(id+"F5.opExtrude","SWEPT_FACE",FACE,{"disambiguationData":[OSD([sQuery(id+"F4.wireOp",EDGE,"E35.filletArc")])]})])],"derivedFrom":makeQuery(id+"F5.opExtrude","CAP_EDGE",EDGE,{"disambiguationData":[OSD([subQ0])],"isStart":false})});}
            var Q4;
            {var subQ0=sQuery(id+"F0.wireOp",EDGE,"E25.7");var subQ1=sQuery(id+"F0.wireOp",EDGE,"E25.1");var subQ2=sQuery(id+"F0.wireOp",EDGE,"E25.6");var subQ3=sQuery(id+"F0.wireOp",EDGE,"E25.5");var subQ4=sQuery(id+"F0.wireOp",EDGE,"E25.4");var subQ5=sQuery(id+"F0.wireOp",EDGE,"E25.0");var subQ6=sQuery(id+"F0.wireOp",EDGE,"E25.2");var subQ7=sQuery(id+"F0.wireOp",EDGE,"E25.3");Q4=makeQuery(id+"F8.boolean.opBoolean","INTERSECT",EDGE,{"derivedFrom":[makeQuery(id+"F5.boolean.opBoolean","SPLIT",FACE,{"disambiguationData":[TD([makeQuery(id+"F2.opExtrude","SWEPT_FACE",FACE,{"disambiguationData":[OSD([subQ5])]})])],"derivedFrom":makeQuery(id+"F3.boolean.opBoolean","COPY",FACE,{"derivedFrom":makeQuery(id+"F3.opExtrude","CAP_FACE",FACE,{"disambiguationData":[OSD([subQ5,subQ1,subQ6,subQ7,subQ4,subQ3,subQ2,subQ0])],"isStart":false})})}),makeQuery(id+"F8.opExtrude","SWEPT_FACE",FACE,{"disambiguationData":[OSD([sQuery(id+"F7.wireOp",EDGE,"E67")])]})]});}
            var Q5;
            Q5=makeQuery(id+"F8.boolean.opBoolean","INTERSECT",EDGE,{"disambiguationData":[OD(0.0)],"derivedFrom":[makeQuery(id+"F5.opExtrude","SWEPT_FACE",FACE,{"disambiguationData":[OSD([sQuery(id+"F4.wireOp",EDGE,"E30")])]}),makeQuery(id+"F8.opExtrude","SWEPT_FACE",FACE,{"disambiguationData":[OSD([sQuery(id+"F7.wireOp",EDGE,"E67")])]})]});
            fillet(context, id + "F14", {"entities" : qUnion([Q0, Q1, Q2, Q3, Q4, Q5]), "radius" : 3 * mm, "tangentPropagation" : true, "allowEdgeOverflow" : false});
        }
        {
            var Q0;
            Q0=makeQuery(id+"F1.opExtrude","CAP_EDGE",EDGE,{"disambiguationData":[OSD([sQuery(id+"F0.wireOp",EDGE,"E1.bottom")])],"isStart":false});
            fillet(context, id + "F15", {"entities" : qUnion([Q0]), "radius" : 2 * mm, "tangentPropagation" : true, "allowEdgeOverflow" : false});
        }
        {
            var Q0;
            {var subQ0=sQuery(id+"F0.wireOp",EDGE,"E21.filletArc");var subQ1=sQuery(id+"F0.wireOp",EDGE,"E7");var subQ2=sQuery(id+"F0.wireOp",EDGE,"E6");var subQ3=sQuery(id+"F0.wireOp",EDGE,"E5");var subQ4=sQuery(id+"F0.wireOp",EDGE,"E4");var subQ5=sQuery(id+"F0.wireOp",EDGE,"E22.filletArc");var subQ6=sQuery(id+"F0.wireOp",EDGE,"E1.bottom");var subQ7=sQuery(id+"F0.wireOp",EDGE,"E1.right");var subQ8=sQuery(id+"F0.wireOp",EDGE,"E1.top");var subQ9=sQuery(id+"F0.wireOp",EDGE,"E1.left");var subQ10=sQuery(id+"F0.wireOp",EDGE,"E23.filletArc");var subQ11=sQuery(id+"F0.wireOp",EDGE,"E24.filletArc");Q0=makeQuery(id+"F2.boolean.opBoolean","SPLIT",FACE,{"disambiguationData":[TD([makeQuery(id+"F1.opExtrude","SWEPT_FACE",FACE,{"disambiguationData":[OSD([subQ6])]})])],"derivedFrom":makeQuery(id+"F1.opExtrude","CAP_FACE",FACE,{"disambiguationData":[OSD([subQ6,subQ8,subQ9,subQ7,subQ4,subQ3,subQ2,subQ1,subQ0,subQ5,subQ10,subQ11])],"isStart":true})});}
            var sketch = newSketch(context, id + "F16", { "sketchPlane" : qUnion([Q0])});
            skLineSegment(sketch, "E79.0", {"start": v(-70, 90) * mm, "end": v(70, 90) * mm});
            skArc(sketch, "E79.1", {"start": v(-70, 90) * mm, "mid": v(-77.07, 87.07) * mm, "end": v(-80, 80) * mm});
            skLineSegment(sketch, "E79.2", {"start": v(-80, -80) * mm, "end": v(-80, 80) * mm});
            skArc(sketch, "E79.3", {"start": v(-80, -80) * mm, "mid": v(-77.07, -87.07) * mm, "end": v(-70, -90) * mm});
            skLineSegment(sketch, "E79.4", {"start": v(-70, -90) * mm, "end": v(70, -90) * mm});
            skArc(sketch, "E79.5", {"start": v(70, -90) * mm, "mid": v(77.07, -87.07) * mm, "end": v(80, -80) * mm});
            skLineSegment(sketch, "E79.6", {"start": v(80, -80) * mm, "end": v(80, 80) * mm});
            skArc(sketch, "E79.7", {"start": v(80, 80) * mm, "mid": v(77.07, 87.07) * mm, "end": v(70, 90) * mm});
            skCircle(sketch, "E79.8", {"center": v(60, 67.5) * mm, "radius": 4 * mm});
            skCircle(sketch, "E79.9", {"center": v(-60, 67.5) * mm, "radius": 4 * mm});
            skCircle(sketch, "E79.10", {"center": v(-60, -67.5) * mm, "radius": 4 * mm});
            skCircle(sketch, "E79.11", {"center": v(60, -67.5) * mm, "radius": 4 * mm});
            skArc(sketch, "E79.12", {"start": v(-56.15, -48.18) * mm, "mid": v(0, -67.5) * mm, "end": v(56.15, -48.18) * mm});
            skLineSegment(sketch, "E79.13", {"start": v(60, 40.3) * mm, "end": v(60, -40.3) * mm});
            skArc(sketch, "E79.14", {"start": v(56.15, -48.18) * mm, "mid": v(58.99, -44.68) * mm, "end": v(60, -40.3) * mm});
            skArc(sketch, "E79.15", {"start": v(-60, -40.3) * mm, "mid": v(-58.99, -44.68) * mm, "end": v(-56.15, -48.18) * mm});
            skLineSegment(sketch, "E79.16", {"start": v(-60, 40.3) * mm, "end": v(-60, -40.3) * mm});
            skArc(sketch, "E79.17", {"start": v(-56.15, 48.18) * mm, "mid": v(-58.99, 44.68) * mm, "end": v(-60, 40.3) * mm});
            skArc(sketch, "E79.18", {"start": v(56.15, 48.18) * mm, "mid": v(0, 67.5) * mm, "end": v(-56.15, 48.18) * mm});
            skArc(sketch, "E79.19", {"start": v(60, 40.3) * mm, "mid": v(58.99, 44.68) * mm, "end": v(56.15, 48.18) * mm});
            skLineSegment(sketch, "E80", {"start": v(0, 90) * mm, "end": v(0, 120) * mm, "construction": true});
            skLineSegment(sketch, "E81", {"start": v(-33, 90) * mm, "end": v(-15, 108) * mm});
            skLineSegment(sketch, "E82", {"start": v(33, 90) * mm, "end": v(15, 108) * mm});
            skCircle(sketch, "E83", {"center": v(0, 120) * mm, "radius": 6 * mm});
            skLineSegment(sketch, "E84", {"start": v(-15, 108) * mm, "end": v(-15, 120) * mm});
            skLineSegment(sketch, "E85", {"start": v(15, 108) * mm, "end": v(15, 120) * mm});
            skArc(sketch, "E86", {"start": v(15, 120) * mm, "mid": v(0, 135) * mm, "end": v(-15, 120) * mm});
            skLineSegment(sketch, "E87", {"start": v(-80, 0) * mm, "end": v(80, 0) * mm, "construction": true});
            skLineSegment(sketch, "E88.MirrorCS", {"start": v(0, -90) * mm, "end": v(0, -120) * mm, "construction": true});
            skLineSegment(sketch, "E89.MirrorCS", {"start": v(33, -90) * mm, "end": v(15, -108) * mm});
            skLineSegment(sketch, "E90.MirrorCS", {"start": v(-15, -108) * mm, "end": v(-15, -120) * mm});
            skArc(sketch, "E91.MirrorCS", {"start": v(15, -120) * mm, "mid": v(0, -135) * mm, "end": v(-15, -120) * mm});
            skLineSegment(sketch, "E92.MirrorCS", {"start": v(15, -108) * mm, "end": v(15, -120) * mm});
            skLineSegment(sketch, "E93.MirrorCS", {"start": v(-33, -90) * mm, "end": v(-15, -108) * mm});
            skCircle(sketch, "E94.MirrorC", {"center": v(0, -120) * mm, "radius": 6 * mm});
            skSolve(sketch);
        }
        {
            var Q0;
            {var subQ1=sQuery(id+"F16.wireOp",EDGE,"E81");Q0=makeQuery(id+"F16.imprint","IMPRINT",FACE,{"disambiguationData":[TD([[makeQuery(id+"F16.imprint","IMPRINT",EDGE,{"derivedFrom":subQ1}),-1.0]])]});}
            var Q1;
            {var subQ1=sQuery(id+"F16.wireOp",EDGE,"E79.1");Q1=makeQuery(id+"F16.imprint","IMPRINT",FACE,{"disambiguationData":[TD([[makeQuery(id+"F16.imprint","IMPRINT",EDGE,{"derivedFrom":subQ1}),1.0]])]});}
            var Q2;
            {var subQ0=sQuery(id+"F16.wireOp",EDGE,"E89.MirrorCS");Q2=makeQuery(id+"F16.imprint","IMPRINT",FACE,{"disambiguationData":[TD([[makeQuery(id+"F16.imprint","IMPRINT",EDGE,{"derivedFrom":subQ0}),-1.0]])]});}
            var Q3;
            Q3=makeQuery(id+"F2.opExtrude","CAP_FACE",FACE,{"disambiguationData":[OSD([sQuery(id+"F0.wireOp",EDGE,"E12"),sQuery(id+"F0.wireOp",EDGE,"E13"),sQuery(id+"F0.wireOp",EDGE,"E14"),sQuery(id+"F0.wireOp",EDGE,"E15"),sQuery(id+"F0.wireOp",EDGE,"E17.filletArc"),sQuery(id+"F0.wireOp",EDGE,"E18.filletArc"),sQuery(id+"F0.wireOp",EDGE,"E19.filletArc"),sQuery(id+"F0.wireOp",EDGE,"E20.filletArc"),sQuery(id+"F0.wireOp",EDGE,"E25.0"),sQuery(id+"F0.wireOp",EDGE,"E25.1"),sQuery(id+"F0.wireOp",EDGE,"E25.2"),sQuery(id+"F0.wireOp",EDGE,"E25.3"),sQuery(id+"F0.wireOp",EDGE,"E25.4"),sQuery(id+"F0.wireOp",EDGE,"E25.5"),sQuery(id+"F0.wireOp",EDGE,"E25.6"),sQuery(id+"F0.wireOp",EDGE,"E25.7")])],"isStart":false});
            extrude(context, id + "F17", {"entities" : qUnion([Q0, Q1, Q2]), "endBound" : BoundingType.UP_TO_SURFACE, "depth" : 25 * mm, "endBoundEntityFace" : qUnion([Q3]), "offsetDistance" : 25 * mm});
        }
    });
